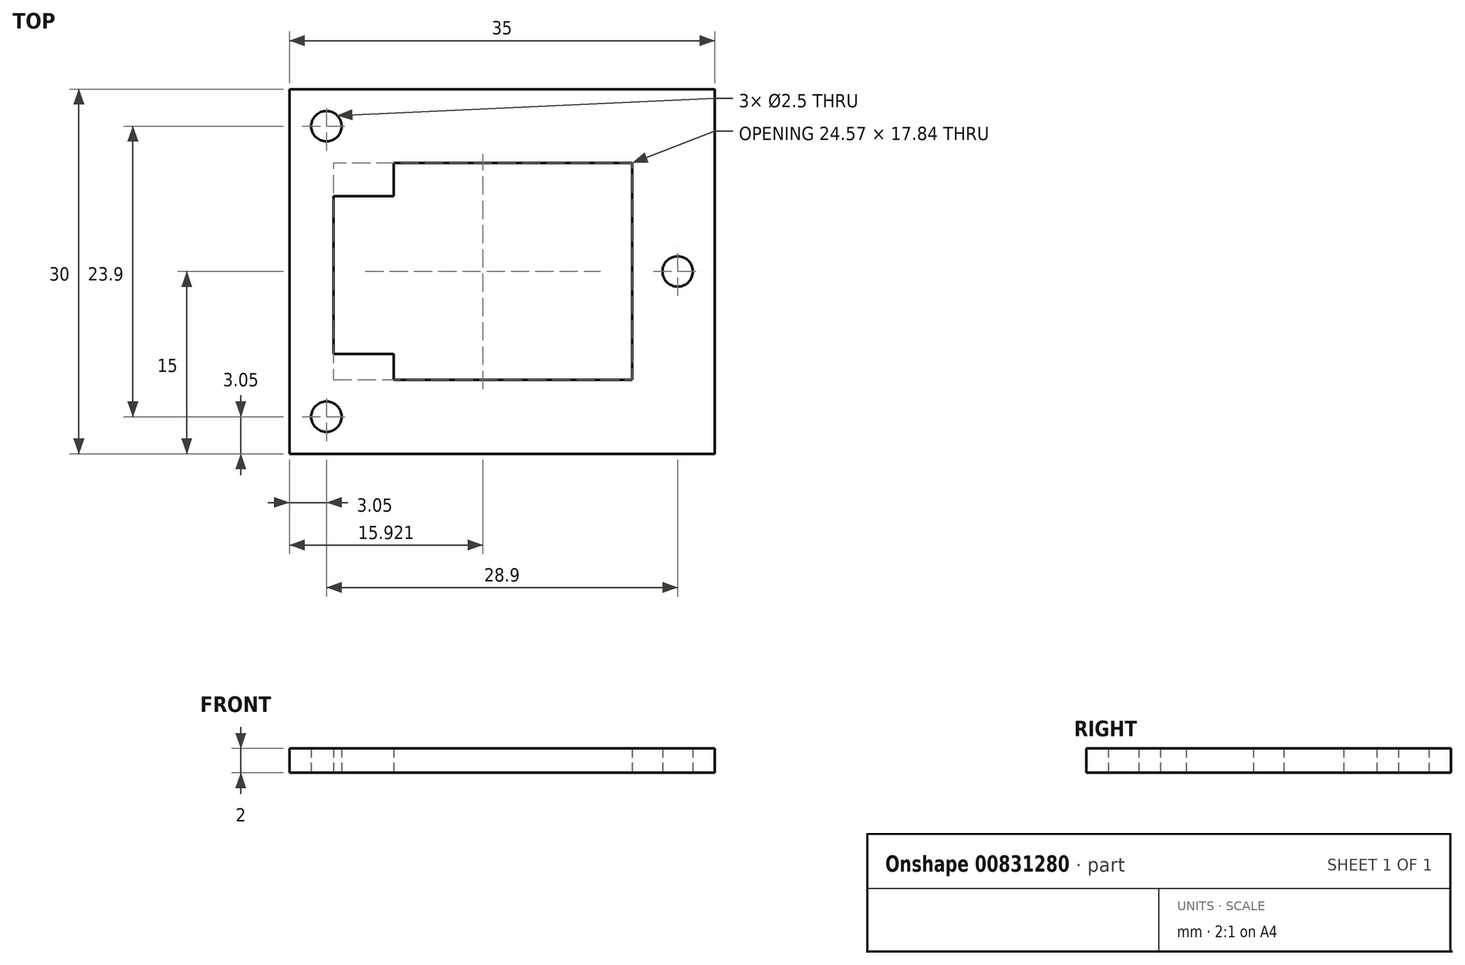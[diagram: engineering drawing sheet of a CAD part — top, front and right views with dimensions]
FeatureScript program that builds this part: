
annotation { "Feature Type Name" : "Feature", "Feature Type Description" : "" }
export const myFeature = defineFeature(function(context is Context, id is Id, definition is map)
    precondition{}
    {
        {
            var Q0;
            Q0=qCreatedBy(makeId("Top.planeOp"),FACE);
            var sketch = newSketch(context, id + "F0", { "sketchPlane" : qUnion([Q0])});
            skLineSegment(sketch, "E0.bottom", {"start": v(17.5, 15) * mm, "end": v(-17.5, 15) * mm});
            skLineSegment(sketch, "E0.top", {"start": v(17.5, -15) * mm, "end": v(-17.5, -15) * mm});
            skLineSegment(sketch, "E0.left", {"start": v(17.5, 15) * mm, "end": v(17.5, -15) * mm});
            skLineSegment(sketch, "E0.right", {"start": v(-17.5, 15) * mm, "end": v(-17.5, -15) * mm});
            skPoint(sketch, "E0.middle", {"position": v(0, 0) * mm});
            skCircle(sketch, "E1", {"center": v(-14.45, 11.95) * mm, "radius": 1.25 * mm});
            skCircle(sketch, "E2", {"center": v(-14.45, -11.95) * mm, "radius": 1.25 * mm});
            skCircle(sketch, "E3", {"center": v(14.45, 0) * mm, "radius": 1.25 * mm});
            skLineSegment(sketch, "E4.bottom", {"start": v(8.92, 8.92) * mm, "end": v(-8.92, 8.92) * mm});
            skLineSegment(sketch, "E4.top", {"start": v(8.92, -8.92) * mm, "end": v(-8.92, -8.92) * mm});
            skLineSegment(sketch, "E4.left", {"start": v(8.92, 8.92) * mm, "end": v(8.92, -8.92) * mm});
            skLineSegment(sketch, "E4.right", {"start": v(-8.92, 8.92) * mm, "end": v(-8.92, -8.92) * mm});
            skLineSegment(sketch, "E5", {"start": v(-8.92, 6.19) * mm, "end": v(-13.86, 6.19) * mm});
            skLineSegment(sketch, "E6", {"start": v(-13.86, 6.19) * mm, "end": v(-13.86, -6.78) * mm});
            skLineSegment(sketch, "E7", {"start": v(-13.86, -6.78) * mm, "end": v(-8.92, -6.78) * mm});
            skLineSegment(sketch, "E8", {"start": v(8.92, 8.92) * mm, "end": v(10.7, 8.92) * mm});
            skLineSegment(sketch, "E9", {"start": v(8.92, -8.92) * mm, "end": v(10.7, -8.92) * mm});
            skLineSegment(sketch, "E10", {"start": v(10.7, 8.92) * mm, "end": v(10.7, -8.92) * mm});
            skSolve(sketch);
        }
        {
            var Q0;
            Q0=qSketchRegion(id+"F0",true);
            extrude(context, id + "F1", {"entities" : qUnion([Q0]), "depth" : 2 * mm, "offsetDistance" : 25.4 * mm});
        }
    });
